# Revit family: Circular_Stools_BIM
name_source: partatom
category: Arredi
units: mm (PartAtom-declared; Revit-internal decimal feet)

## family parameters
Attiva taglio nelle viste = No
Basato su piano di lavoro = No
Condiviso = No
Numero OmniClass = 23.40.20.00
Origine composizione di rendering = Geometria famiglia
Punto di calcolo locali = No
Sempre verticale = Sì
Taglio con vuoti quando caricato = No
Titolo OmniClass = General Furniture and Specialties

## types (3) — shared parameters
AVAILABLE FINISHES = Black powder coat finish (BP), or satin nickel (SN), satin brass (SB), bronze (BZ) or gunmetal (GM) nanoceramic coated tubular steel.
BASE MATERIAL = BASSAM_FELLOWS_COACH_LEATHER_11073_PLAEGRAY
BIM BADGE = https://bim.archiproducts.com
COLLECTION = CIRCULAR
MATERIAL DESCRIPTION = Tubular stainless steel base. Foam upholstery with double topstitch. CARB2 plywood inner frame.
PRODUCT SHEET = https://www.archiproducts.com
Produttore = BassamFellows
STRUCTURE MATERIAL = BASSAM_FELLOWS_MATT_BLACK_BP
TECHNICAL SHEET = https://bassamfellows.com
URL = https://bassamfellows.com
WEIGHT = 0.00 kg
zero-valued in all types: Prospetto di default

## per-type parameters (varying)
| type | CB-260 VISIBILITY | CB-262 VISIBILITY | CB-263 VISIBILITY | DIAMETER | Descrizione | HEIGHT | Modello | SEAT 40 cm VISIBILITY | height leg |
| CB-260 | Sì | No | No | 450 mm  [stored 1.47638 ft] | Upholstered stool with steel base | 460 mm | Circular Stool | No | 400 mm  [stored 1.31234 ft] |
| CB-262 | No | Sì | No | 400 mm  [stored 1.31234 ft] | Upholstered counter stool with steel base | 650 mm | Circular Counter Stool | Sì | 590 mm  [stored 1.9357 ft] |
| CB-263 | No | No | Sì | 400 mm  [stored 1.31234 ft] | Upholstered bar stool with steel base | 804 mm  [stored 2.6378 ft] | Circular Bar Stool | Sì | 744 mm  [stored 2.44094 ft] |

note: column(s) folded — value = type name in every type: PRODUCT CODE

note: [stored X ft] marks values corroborated as IEEE doubles in the binary element streams (Revit-internal decimal feet)

## geometry (parser evidence)
native form markers: Sweep x2
no freeform markers — native parametric forms only
